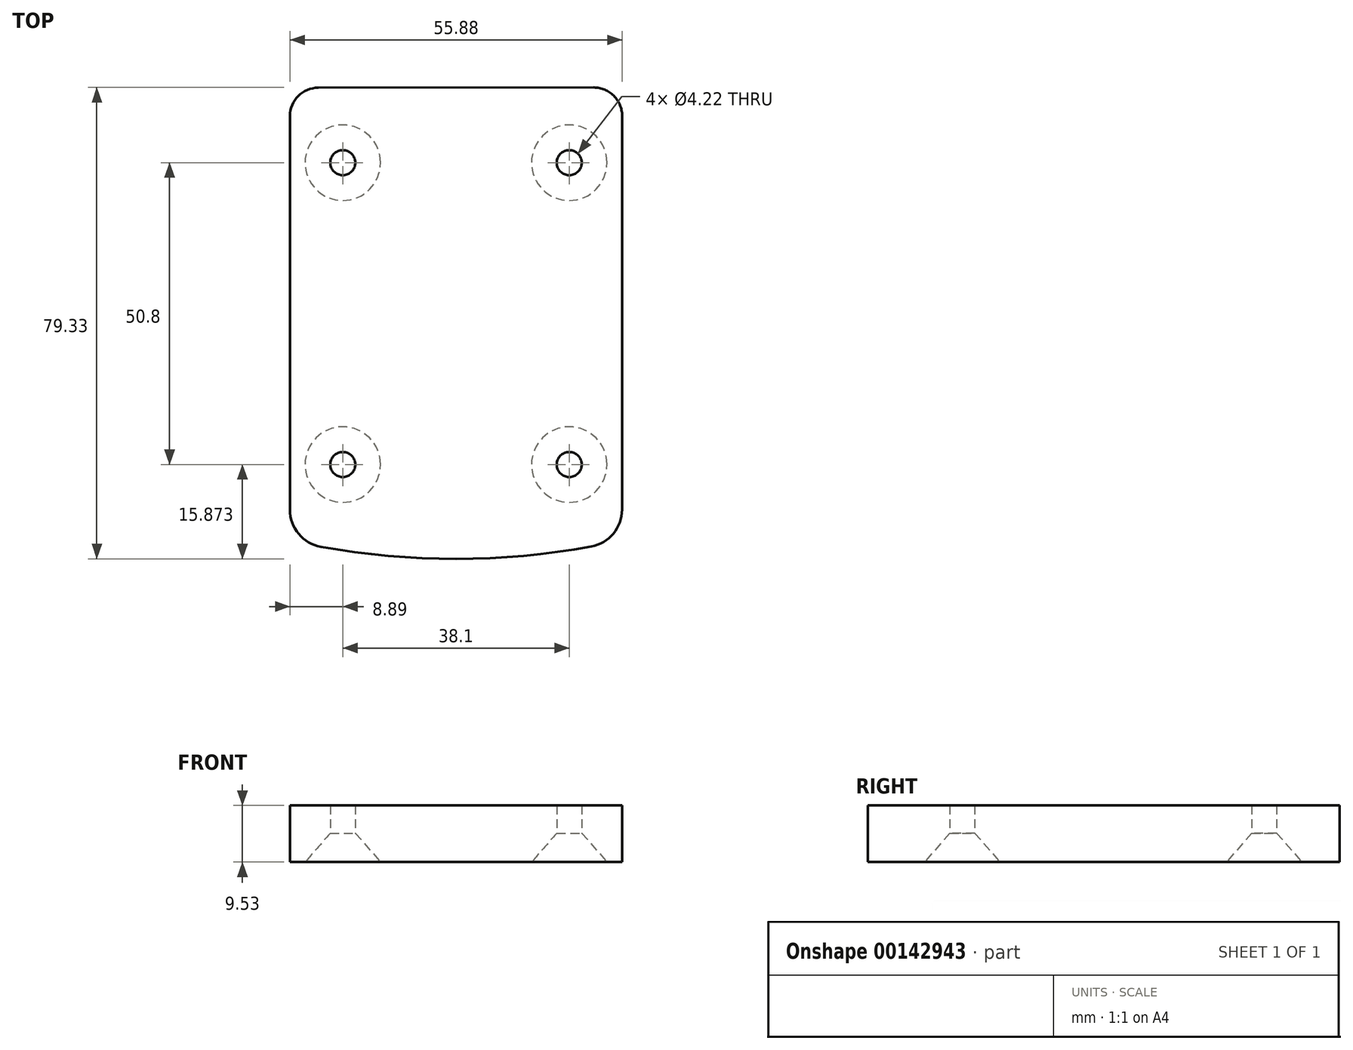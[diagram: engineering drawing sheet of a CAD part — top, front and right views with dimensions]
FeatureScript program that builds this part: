
annotation { "Feature Type Name" : "Feature", "Feature Type Description" : "" }
export const myFeature = defineFeature(function(context is Context, id is Id, definition is map)
    precondition{}
    {
        {
            var Q0;
            Q0=qCreatedBy(makeId("Top.planeOp"),FACE);
            var sketch = newSketch(context, id + "F0", { "sketchPlane" : qUnion([Q0])});
            skLineSegment(sketch, "E0.bottom", {"start": v(23.17, 38.12) * mm, "end": v(-23.18, 38.08) * mm});
            skLineSegment(sketch, "E0.left", {"start": v(27.94, 33.36) * mm, "end": v(27.94, -32.9) * mm});
            skLineSegment(sketch, "E0.right", {"start": v(-27.94, 33.32) * mm, "end": v(-27.94, -32.93) * mm});
            skPoint(sketch, "E0.middle", {"position": v(0, 0) * mm});
            skArc(sketch, "E1", {"start": v(-22.72, -39.18) * mm, "mid": v(0, -41.21) * mm, "end": v(22.73, -39.14) * mm});
            skLineSegment(sketch, "E2", {"start": v(0, -41.21) * mm, "end": v(0, 38.1) * mm, "construction": true});
            skLineSegment(sketch, "E3", {"start": v(-27.94, -0.02) * mm, "end": v(27.94, 0.02) * mm, "construction": true});
            skPoint(sketch, "E4", {"position": v(-19.05, 25.46) * mm});
            skPoint(sketch, "E5", {"position": v(19.05, 25.46) * mm});
            skPoint(sketch, "E6", {"position": v(-19.05, -25.34) * mm});
            skPoint(sketch, "E7", {"position": v(19.05, -25.34) * mm});
            skPoint(sketch, "E8.visualSharp", {"position": v(-27.94, 38.08) * mm});
            skArc(sketch, "E8.filletArc", {"start": v(-23.18, 38.08) * mm, "mid": v(-26.55, 36.69) * mm, "end": v(-27.94, 33.32) * mm});
            skPoint(sketch, "E9.visualSharp", {"position": v(27.94, 38.12) * mm});
            skArc(sketch, "E9.filletArc", {"start": v(27.94, 33.36) * mm, "mid": v(26.54, 36.72) * mm, "end": v(23.17, 38.12) * mm});
            skPoint(sketch, "E10.visualSharp", {"position": v(27.94, -38.08) * mm});
            skArc(sketch, "E10.filletArc", {"start": v(22.73, -39.14) * mm, "mid": v(26.47, -36.96) * mm, "end": v(27.94, -32.9) * mm});
            skPoint(sketch, "E11.visualSharp", {"position": v(-27.94, -38.12) * mm});
            skArc(sketch, "E11.filletArc", {"start": v(-27.94, -32.93) * mm, "mid": v(-26.46, -37) * mm, "end": v(-22.72, -39.18) * mm});
            skLineSegment(sketch, "E12", {"start": v(-52.4, 54.48) * mm, "end": v(-52.4, 5.51) * mm, "construction": true});
            skLineSegment(sketch, "E13", {"start": v(-101.6, 5.51) * mm, "end": v(-101.6, 140.03) * mm, "construction": true});
            skLineSegment(sketch, "E14", {"start": v(-139.7, 140.03) * mm, "end": v(-139.7, 24.12) * mm, "construction": true});
            skLineSegment(sketch, "E15", {"start": v(-53.19, -365.06) * mm, "end": v(53.19, -365.06) * mm});
            skLineSegment(sketch, "E16", {"start": v(0, -279.82) * mm, "end": v(0, -441.83) * mm, "construction": true});
            skLineSegment(sketch, "E17", {"start": v(-156.83, 93.73) * mm, "end": v(-23.53, 93.73) * mm, "construction": true});
            skLineSegment(sketch, "E18", {"start": v(-78.6, 39.75) * mm, "end": v(-156.83, 39.75) * mm, "construction": true});
            skLineSegment(sketch, "E19", {"start": v(-247.86, -284.1) * mm, "end": v(58.24, -284.1) * mm, "construction": true});
            skLineSegment(sketch, "E20", {"start": v(-161.92, -440.34) * mm, "end": v(-161.92, -188.2) * mm, "construction": true});
            skArc(sketch, "E21", {"start": v(-161.93, -284.1) * mm, "mid": v(-65.55, -128.03) * mm, "end": v(-139.7, 39.75) * mm, "construction": true});
            skArc(sketch, "E22", {"start": v(-161.93, -284.1) * mm, "mid": v(-120.97, -342.6) * mm, "end": v(-53.19, -365.06) * mm});
            skFitSpline(sketch, "E23", {"points": [v(-52.4, 12.33) * mm, v(-35.79, 22) * mm, v(-26.55, 36.69) * mm], "startDerivative": vector(50.2, 3.3) * mm, "endDerivative": vector(25.97, 20.52) * mm});
            skPoint(sketch, "E24.4.internal.snap0", {"position": v(-101.6, 72.77) * mm});
            skFitSpline(sketch, "E25", {"points": [v(-101.6, 93.73) * mm, v(-120.3, 88.1) * mm, v(-134.7, 66.7) * mm, v(-139.7, 39.75) * mm, v(-115.58, -104.47) * mm, v(-154.95, -239.45) * mm, v(-161.92, -284.1) * mm], "startDerivative": vector(-203.22, -24.1) * mm, "endDerivative": vector(-25.16, -258.4) * mm});
            skFitSpline(sketch, "E26", {"points": [v(-101.6, 93.73) * mm, v(-95.3, 93.73) * mm, v(-81.5, 72.77) * mm, v(-73.95, 33) * mm, v(-64.83, 14.88) * mm, v(-52.4, 12.33) * mm], "startDerivative": vector(52.54, 14.3) * mm, "endDerivative": vector(82.62, -1.48) * mm});
            skSolve(sketch);
        }
        {
            var Q0;
            Q0=makeQuery(id+"F0.imprint","IMPRINT",FACE,{"disambiguationData":[TD([[makeQuery(id+"F0.imprint","IMPRINT",EDGE,{"derivedFrom":sQuery(id+"F0.wireOp",EDGE,"E0.bottom")}),1.0]])]});
            extrude(context, id + "F1", {"entities" : qUnion([Q0]), "depth" : 9.52 * mm});
        }
        {
            var Q0;
            Q0=sQuery(id+"F0.wireOp",VERTEX,"E4");
            var Q1;
            Q1=sQuery(id+"F0.wireOp",VERTEX,"E5");
            var Q2;
            Q2=sQuery(id+"F0.wireOp",VERTEX,"E6");
            var Q3;
            Q3=sQuery(id+"F0.wireOp",VERTEX,"E7");
            var Q4;
            Q4=makeQuery(id+"F1.opExtrude","SWEPT_BODY",BODY,{"disambiguationData":[OSD([sQuery(id+"F0.wireOp",EDGE,"E0.bottom"),sQuery(id+"F0.wireOp",EDGE,"E0.left"),sQuery(id+"F0.wireOp",EDGE,"E0.right"),sQuery(id+"F0.wireOp",EDGE,"E1")])]});
            hole(context, id + "F2", {"style" : HoleStyle.C_SINK, "endStyle" : HoleEndStyle.THROUGH, "oppositeDirection" : true, "holeDiameter" : 4.22 * mm, "cSinkDiameter" : 12.7 * mm, "cSinkAngle" : 82 * degree, "locations" : qUnion([Q0, Q1, Q2, Q3]), "scope" : qUnion([Q4]), "isTappedThrough" : true});
        }
    });
